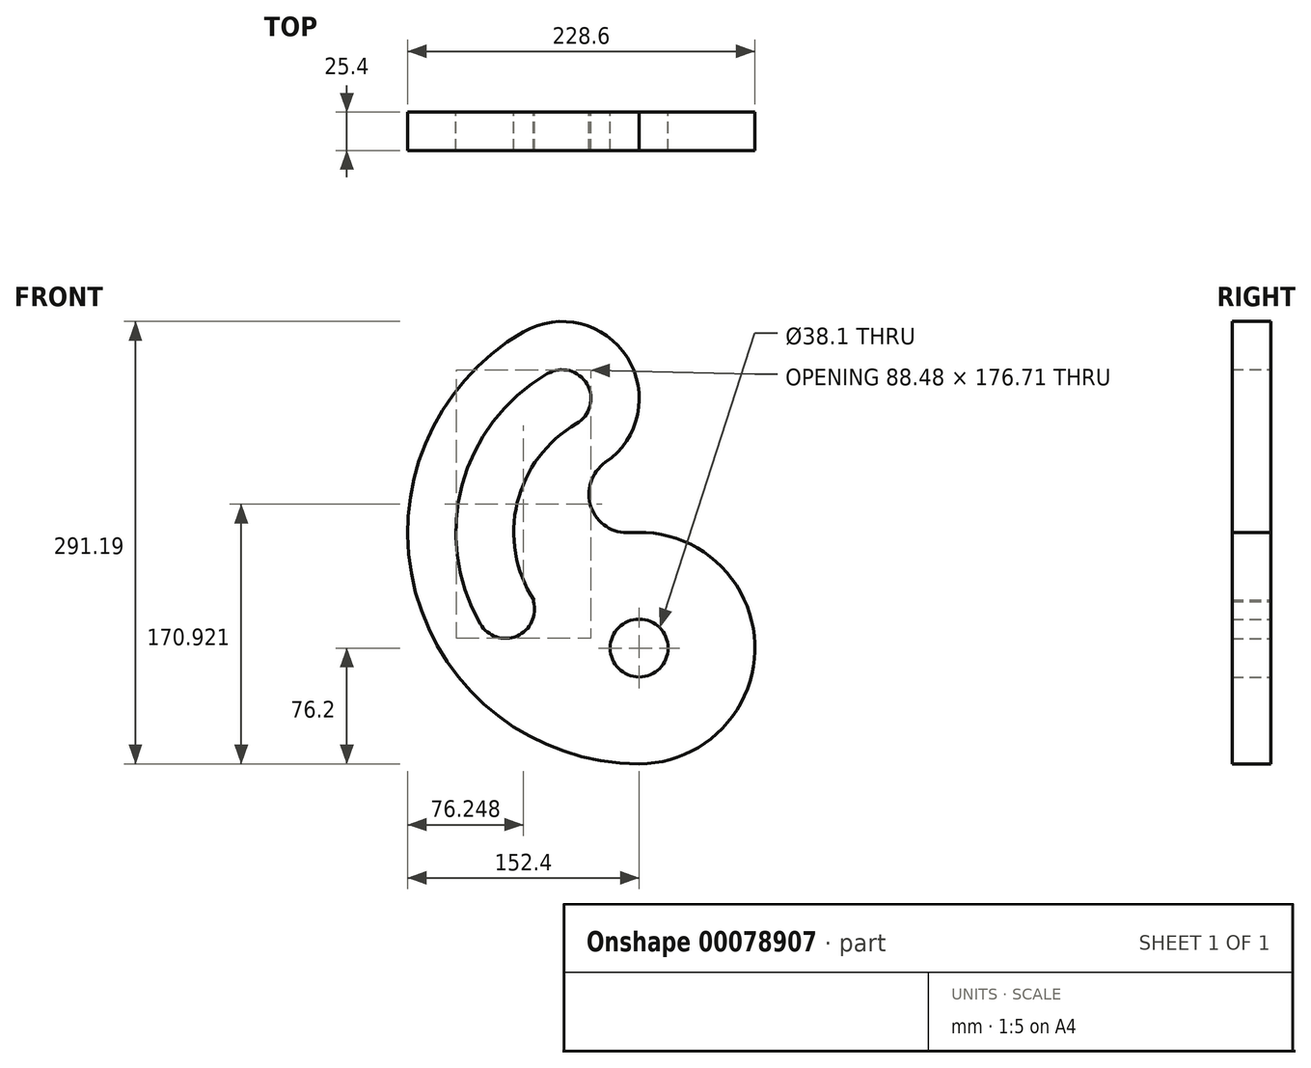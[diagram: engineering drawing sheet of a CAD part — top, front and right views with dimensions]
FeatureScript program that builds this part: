
annotation { "Feature Type Name" : "Feature", "Feature Type Description" : "" }
export const myFeature = defineFeature(function(context is Context, id is Id, definition is map)
    precondition{}
    {
        {
            var Q0;
            Q0=qCreatedBy(makeId("Front.planeOp"),FACE);
            var sketch = newSketch(context, id + "F0", { "sketchPlane" : qUnion([Q0])});
            skCircle(sketch, "E0", {"center": v(0, 0) * mm, "radius": 19.05 * mm});
            skArc(sketch, "E1", {"start": v(0, -76.2) * mm, "mid": v(76.14, 2.91) * mm, "end": v(-5.83, 75.98) * mm});
            skLineSegment(sketch, "E2", {"start": v(0, 0) * mm, "end": v(0, 76.2) * mm, "construction": true});
            skLineSegment(sketch, "E3", {"start": v(0, 76.2) * mm, "end": v(-141.15, -5.3) * mm, "construction": true});
            skArc(sketch, "E4", {"start": v(-60.33, 180.69) * mm, "mid": v(-116.54, 107.43) * mm, "end": v(-104.49, 15.87) * mm});
            skLineSegment(sketch, "E5", {"start": v(0, 76.2) * mm, "end": v(-60.33, 180.69) * mm, "construction": true});
            skArc(sketch, "E6", {"start": v(-104.49, 15.87) * mm, "mid": v(-78.46, 8.9) * mm, "end": v(-71.5, 34.92) * mm});
            skArc(sketch, "E7", {"start": v(-41.28, 147.7) * mm, "mid": v(-34.3, 173.71) * mm, "end": v(-60.33, 180.69) * mm});
            skArc(sketch, "E8", {"start": v(-41.28, 147.7) * mm, "mid": v(-80.23, 95.61) * mm, "end": v(-69.4, 31.49) * mm});
            skArc(sketch, "E9", {"start": v(-76.2, 208.18) * mm, "mid": v(-147.2, 36.76) * mm, "end": v(0, -76.2) * mm});
            skArc(sketch, "E10", {"start": v(-25.4, 120.2) * mm, "mid": v(-6.8, 189.59) * mm, "end": v(-76.2, 208.18) * mm});
            skArc(sketch, "E11", {"start": v(-22.11, 122.26) * mm, "mid": v(-31.73, 92.87) * mm, "end": v(-5.83, 75.98) * mm});
            skArc(sketch, "E12.trimOffspring", {"start": v(-69.4, 31.49) * mm, "mid": v(-69.55, 31.13) * mm, "end": v(-69.71, 30.77) * mm});
            skSolve(sketch);
        }
        {
            var Q0;
            Q0 = qSketchRegion(id + "F0", true);
            extrude(context, id + "F1", {"entities" : qUnion([Q0]), "depth" : 25.4 * mm});
        }
    });
